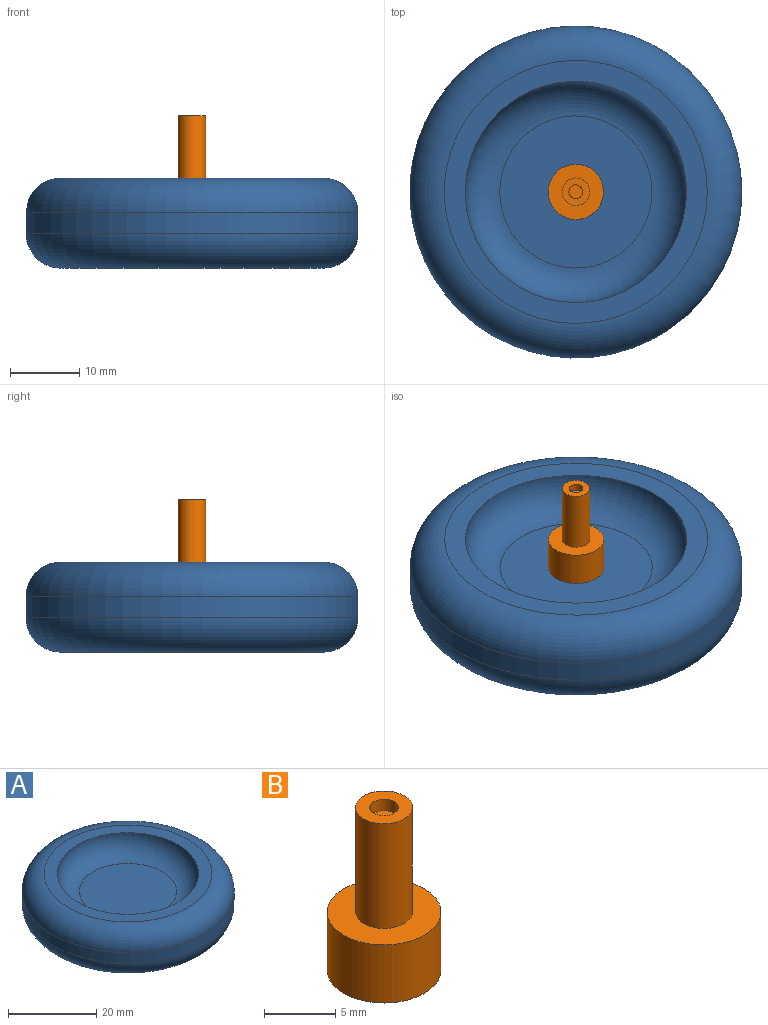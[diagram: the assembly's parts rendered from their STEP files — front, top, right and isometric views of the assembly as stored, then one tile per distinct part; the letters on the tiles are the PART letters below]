
ASSEMBLY  parts=2 mates=1
PART A: 7 faces, bbox 52x52x16.6 mm
  f0: cylinder r=24mm len=48mm, axis (0,0,-1), area 452.4mm2, adj f4,f5
  f1: plane 38x38mm, normal (0,0,1), area 329.9mm2, adj f4,f6
  f2: plane 38x38mm, normal (0,0,-1), area 1134.1mm2, adj f5
  f3: plane 22x22mm, normal (0,0,1), area 380.1mm2, adj f6
  f4: torus R=19mm, axis (0,0,1), area 1094.7mm2, adj f0,f1
  f5: torus R=19mm, axis (0,0,1), area 1094.7mm2, adj f0,f2
  f6: torus R=11mm, axis (0,0,1), area 699.9mm2, adj f1,f3
PART B: 7 faces, bbox 8x8x14 mm
  f0: cylinder r=4mm len=8mm, axis (0,0,-1), area 125.7mm2, adj f1,f2
  f1: plane 8x8mm, normal (0,0,1), area 37.7mm2, adj f0,f3
  f2: plane 8x8mm, normal (0,0,-1), area 50.3mm2, adj f0
  f3: cylinder r=2mm len=9mm, axis (0,0,-1), area 113.1mm2, adj f1,f5
  f4: cylinder r=1mm len=2mm, axis (0,0,-1), area 6.3mm2, adj f5,f6
  f5: plane 4x4mm, normal (0,0,1), area 9.4mm2, adj f3,f4
  f6: plane 2x2mm, normal (0,0,1), area 3.1mm2, adj f4
PLACE A t=(-7.06,-9.74,5.2)mm fixed
PLACE B t=(-14.53,5.93,5.2)mm
MATE slider A.f0 <-> B.f0  axis (0,0,1) through (-10.08,-3.35,5.2)mm
